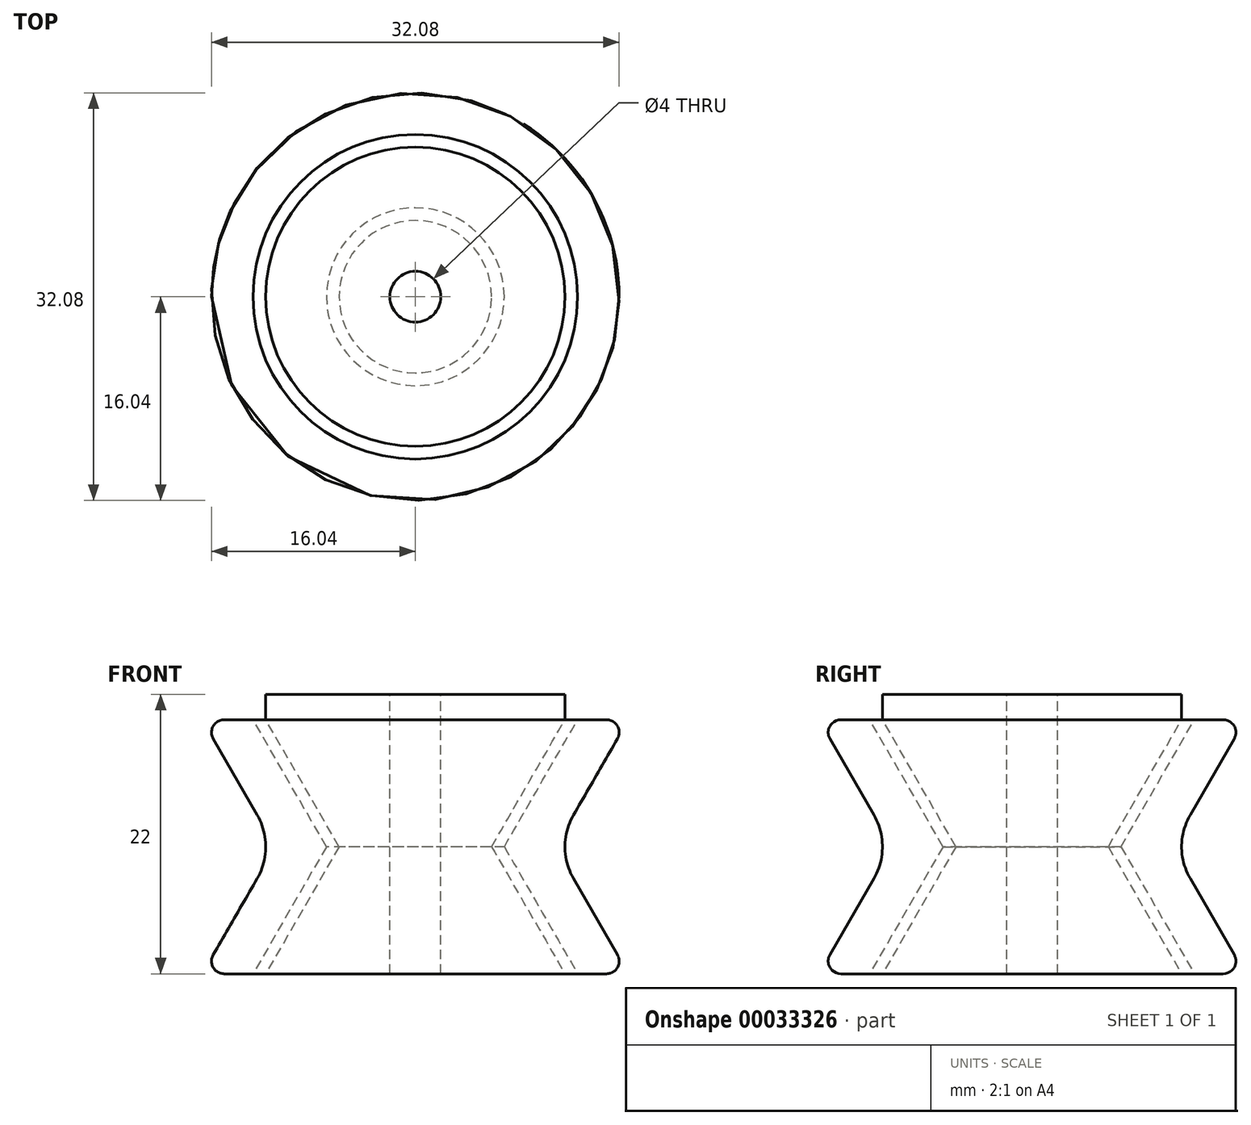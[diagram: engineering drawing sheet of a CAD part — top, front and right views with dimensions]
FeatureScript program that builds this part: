
annotation { "Feature Type Name" : "Feature", "Feature Type Description" : "" }
export const myFeature = defineFeature(function(context is Context, id is Id, definition is map)
    precondition{}
    {
        {
            var Q0;
            Q0=qCreatedBy(makeId("Front.planeOp"),FACE);
            var sketch = newSketch(context, id + "F0", { "sketchPlane" : qUnion([Q0])});
            skLineSegment(sketch, "E0", {"start": v(0, 10) * mm, "end": v(0, -10) * mm, "construction": true});
            skLineSegment(sketch, "E1", {"start": v(-2, 10) * mm, "end": v(2, 10) * mm});
            skLineSegment(sketch, "E2", {"start": v(2, 10) * mm, "end": v(2, -10) * mm});
            skLineSegment(sketch, "E3", {"start": v(2, -10) * mm, "end": v(-2, -10) * mm});
            skLineSegment(sketch, "E4", {"start": v(-2, -10) * mm, "end": v(-2, 10) * mm});
            skLineSegment(sketch, "E5", {"start": v(-11.77, 10) * mm, "end": v(11.77, 10) * mm});
            skLineSegment(sketch, "E6", {"start": v(11.77, 10) * mm, "end": v(6, 0) * mm});
            skLineSegment(sketch, "E7", {"start": v(6, 0) * mm, "end": v(11.77, -10) * mm});
            skLineSegment(sketch, "E8", {"start": v(11.77, -10) * mm, "end": v(2, -10) * mm});
            skLineSegment(sketch, "E9", {"start": v(-11.77, 10) * mm, "end": v(-6, 0) * mm});
            skLineSegment(sketch, "E10", {"start": v(-6, 0) * mm, "end": v(-11.77, -10) * mm});
            skLineSegment(sketch, "E11", {"start": v(-11.77, -10) * mm, "end": v(-2, -10) * mm});
            skLineSegment(sketch, "E12", {"start": v(-11.77, 10) * mm, "end": v(-11.77, -10) * mm, "construction": true});
            skLineSegment(sketch, "E13", {"start": v(11.77, 10) * mm, "end": v(11.77, -10) * mm, "construction": true});
            skLineSegment(sketch, "E14", {"start": v(-6, 0) * mm, "end": v(6, 0) * mm, "construction": true});
            skPoint(sketch, "E15", {"position": v(0, 0) * mm});
            skLineSegment(sketch, "E16", {"start": v(-2, 8) * mm, "end": v(2, 8) * mm, "construction": true});
            skPoint(sketch, "E17", {"position": v(0, 8) * mm});
            skLineSegment(sketch, "E18", {"start": v(-12.77, 10) * mm, "end": v(-7, 0) * mm});
            skLineSegment(sketch, "E19", {"start": v(-7, 0) * mm, "end": v(-12.77, -10) * mm});
            skLineSegment(sketch, "E20", {"start": v(-12.77, -10) * mm, "end": v(-16.77, -10) * mm});
            skPoint(sketch, "E20.endSnap0", {"position": v(-6.89, -10) * mm});
            skLineSegment(sketch, "E21", {"start": v(-16.77, -10) * mm, "end": v(-11, 0) * mm});
            skLineSegment(sketch, "E22", {"start": v(-11, 0) * mm, "end": v(-16.77, 10) * mm});
            skLineSegment(sketch, "E23", {"start": v(-16.77, 10) * mm, "end": v(-12.77, 10) * mm});
            skLineSegment(sketch, "E24", {"start": v(-12.77, 10) * mm, "end": v(-12.77, -10) * mm, "construction": true});
            skLineSegment(sketch, "E25", {"start": v(-11, 0) * mm, "end": v(-7, 0) * mm, "construction": true});
            skLineSegment(sketch, "E26", {"start": v(-11.77, -10) * mm, "end": v(-12.77, -10) * mm, "construction": true});
            skLineSegment(sketch, "E27", {"start": v(-12.77, 10) * mm, "end": v(-11.77, 10) * mm, "construction": true});
            skSolve(sketch);
        }
        {
            var Q0;
            {var subQ1=sQuery(id+"F0.wireOp",EDGE,"E4");Q0=makeQuery(id+"F0.imprint","IMPRINT",FACE,{"disambiguationData":[TD([[makeQuery(id+"F0.imprint","IMPRINT",EDGE,{"derivedFrom":subQ1}),1.0]])]});}
            var Q1;
            Q1=makeQuery(id+"F0.imprint","IMPRINT",FACE,{"disambiguationData":[TD([[makeQuery(id+"F0.imprint","IMPRINT",EDGE,{"derivedFrom":sQuery(id+"F0.wireOp",EDGE,"E18")}),-1.0]])]});
            var Q2;
            Q2=sQuery(id+"F0.wireOp",EDGE,"E0");
            revolve(context, id + "F1", {"entities" : qUnion([Q0, Q1]), "axis" : qUnion([Q2]), "revolveType" : RevolveType.FULL});
        }
        {
            var Q0;
            Q0=makeQuery(id+"F1.opRevolve","SWEPT_EDGE",EDGE,{"disambiguationData":[OSD([sQuery(id+"F0.wireOp",EDGE,"E21"),sQuery(id+"F0.wireOp",EDGE,"E22")])]});
            fillet(context, id + "F2", {"entities" : qUnion([Q0]), "radius" : 5 * mm, "tangentPropagation" : true, "allowEdgeOverflow" : false});
        }
        {
            var Q0;
            Q0=makeQuery(id+"F1.opRevolve","SWEPT_EDGE",EDGE,{"disambiguationData":[OSD([sQuery(id+"F0.wireOp",EDGE,"E22"),sQuery(id+"F0.wireOp",EDGE,"E23")])]});
            var Q1;
            Q1=makeQuery(id+"F1.opRevolve","SWEPT_EDGE",EDGE,{"disambiguationData":[OSD([sQuery(id+"F0.wireOp",EDGE,"E20"),sQuery(id+"F0.wireOp",EDGE,"E21")])]});
            fillet(context, id + "F3", {"entities" : qUnion([Q0, Q1]), "radius" : 1 * mm, "tangentPropagation" : true, "allowEdgeOverflow" : false});
        }
        {
            var Q0;
            Q0=makeQuery(id+"F1.opRevolve","SWEPT_FACE",FACE,{"disambiguationData":[OSD([sQuery(id+"F0.wireOp",EDGE,"E5")])]});
            extrude(context, id + "F4", {"entities" : qUnion([Q0]), "operationType" : NewBodyOperationType.ADD, "depth" : 2 * mm});
        }
    });
